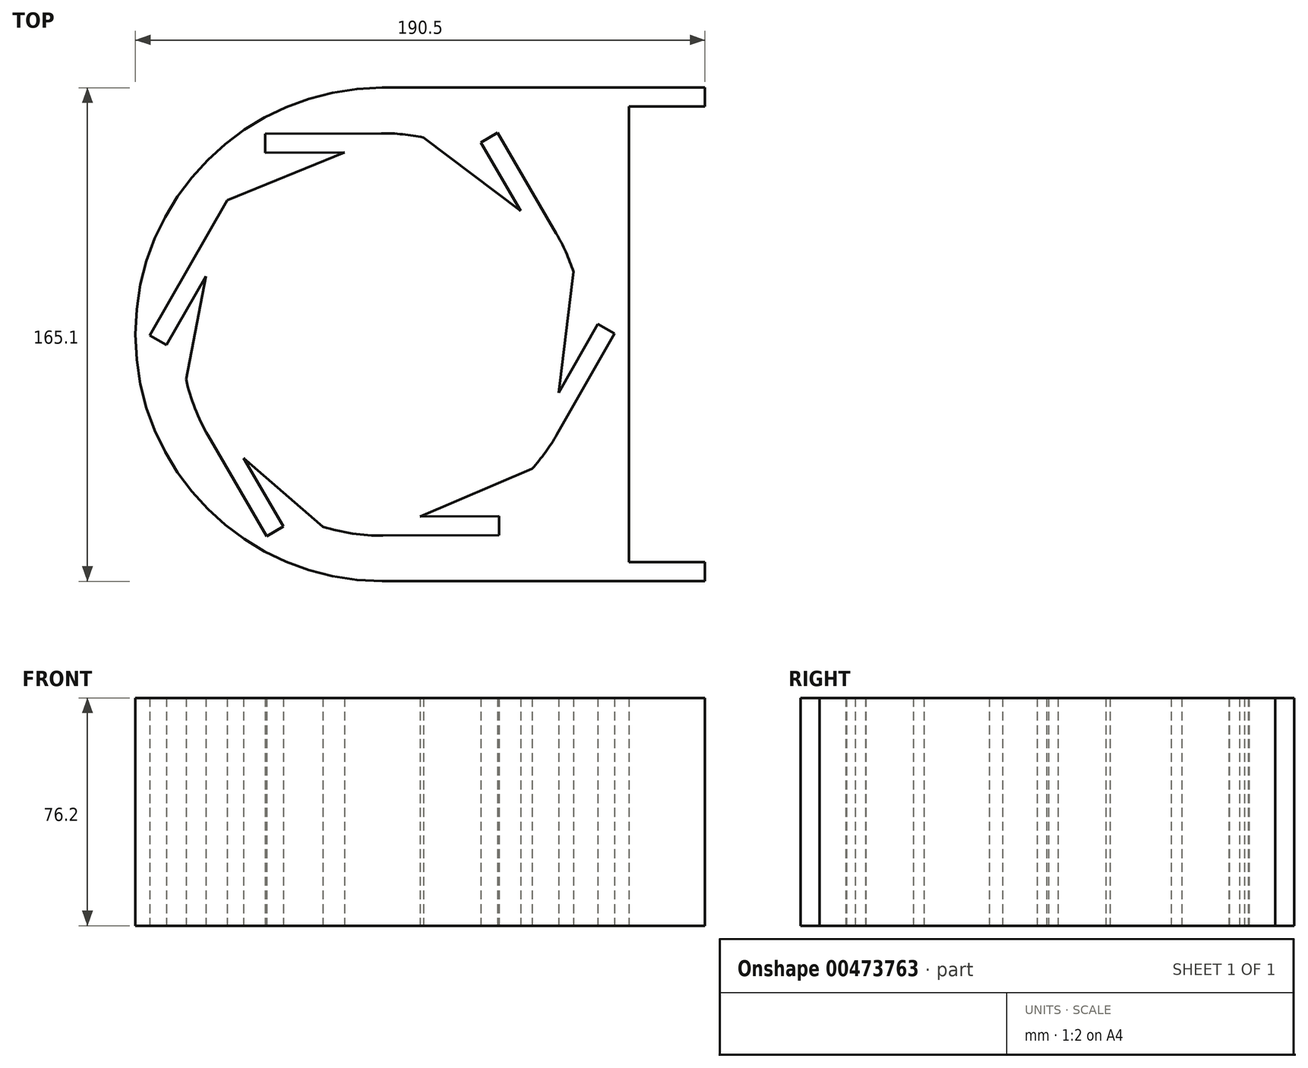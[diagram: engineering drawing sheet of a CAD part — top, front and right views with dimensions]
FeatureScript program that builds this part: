
annotation { "Feature Type Name" : "Feature", "Feature Type Description" : "" }
export const myFeature = defineFeature(function(context is Context, id is Id, definition is map)
    precondition{}
    {
        {
            var Q0;
            Q0=qCreatedBy(makeId("Top.planeOp"),FACE);
            var sketch = newSketch(context, id + "F0", { "sketchPlane" : qUnion([Q0])});
            skArc(sketch, "E0", {"start": v(-65.63, -17.73) * mm, "mid": v(-62.61, -27.48) * mm, "end": v(-58.16, -36.65) * mm});
            skArc(sketch, "E1.cCircle", {"start": v(-65.63, -17.73) * mm, "mid": v(-62.61, -27.48) * mm, "end": v(-58.16, -36.65) * mm, "construction": true});
            skLineSegment(sketch, "E1.0", {"start": v(38.6, 64.7) * mm, "end": v(58.16, 31.12) * mm});
            skLineSegment(sketch, "E1.1", {"start": v(77.72, -2.46) * mm, "end": v(58.42, -36.2) * mm});
            skLineSegment(sketch, "E1.2", {"start": v(39.13, -69.92) * mm, "end": v(0.27, -70.08) * mm});
            skLineSegment(sketch, "E1.3", {"start": v(-38.6, -70.23) * mm, "end": v(-58.16, -36.65) * mm});
            skLineSegment(sketch, "E1.4", {"start": v(-77.72, -3.07) * mm, "end": v(-51.86, 42.14) * mm});
            skLineSegment(sketch, "E1.5", {"start": v(-39.13, 64.39) * mm, "end": v(-0.27, 64.54) * mm});
            skPoint(sketch, "E1.0.midPoint", {"position": v(58.16, 31.12) * mm});
            skLineSegment(sketch, "E2", {"start": v(38.6, 64.7) * mm, "end": v(33.04, 61.46) * mm});
            skLineSegment(sketch, "E3", {"start": v(33.04, 61.46) * mm, "end": v(46.37, 38.6) * mm});
            skLineSegment(sketch, "E4", {"start": v(50.92, 41.25) * mm, "end": v(51.92, 41.83) * mm});
            skLineSegment(sketch, "E5", {"start": v(-39.13, 64.39) * mm, "end": v(-39.1, 57.96) * mm});
            skLineSegment(sketch, "E6", {"start": v(-39.1, 57.96) * mm, "end": v(-12.64, 58.07) * mm});
            skLineSegment(sketch, "E7", {"start": v(-12.64, 63.35) * mm, "end": v(-12.64, 64.5) * mm});
            skLineSegment(sketch, "E8", {"start": v(-12.64, 64.5) * mm, "end": v(-39.13, 64.39) * mm});
            skLineSegment(sketch, "E9", {"start": v(-77.72, -3.07) * mm, "end": v(-72.14, -6.26) * mm});
            skLineSegment(sketch, "E10", {"start": v(-72.14, -6.26) * mm, "end": v(-59, 16.7) * mm});
            skLineSegment(sketch, "E11", {"start": v(-63.58, 19.33) * mm, "end": v(-64.58, 19.9) * mm});
            skLineSegment(sketch, "E12", {"start": v(-38.6, -70.23) * mm, "end": v(-33.04, -67) * mm});
            skLineSegment(sketch, "E13", {"start": v(-33.04, -67) * mm, "end": v(-46.37, -44.13) * mm});
            skLineSegment(sketch, "E14", {"start": v(-50.92, -46.78) * mm, "end": v(-51.92, -47.36) * mm});
            skLineSegment(sketch, "E15", {"start": v(39.13, -69.92) * mm, "end": v(39.1, -63.5) * mm});
            skLineSegment(sketch, "E16", {"start": v(39.1, -63.5) * mm, "end": v(12.64, -63.6) * mm});
            skLineSegment(sketch, "E17", {"start": v(12.66, -68.88) * mm, "end": v(12.66, -70.03) * mm});
            skLineSegment(sketch, "E18", {"start": v(77.72, -2.46) * mm, "end": v(72.14, 0.73) * mm});
            skLineSegment(sketch, "E19", {"start": v(72.14, 0.73) * mm, "end": v(59, -22.24) * mm});
            skLineSegment(sketch, "E20", {"start": v(63.58, -24.86) * mm, "end": v(64.58, -25.43) * mm});
            skArc(sketch, "E21", {"start": v(0, 79.78) * mm, "mid": v(-82.55, -2.77) * mm, "end": v(0, -85.32) * mm});
            skArc(sketch, "E22.trimOffspring", {"start": v(-49.12, 43.25) * mm, "mid": v(-49.64, 42.7) * mm, "end": v(-50.14, 42.14) * mm, "construction": true});
            skArc(sketch, "E23.trimOffspring", {"start": v(13.83, 63.1) * mm, "mid": v(6.82, 64.2) * mm, "end": v(-0.27, 64.54) * mm, "construction": true});
            skArc(sketch, "E24.trimOffspring", {"start": v(13.83, 63.1) * mm, "mid": v(6.82, 64.2) * mm, "end": v(-0.27, 64.54) * mm});
            skArc(sketch, "E25.trimOffspring", {"start": v(-49.12, 43.25) * mm, "mid": v(-49.64, 42.7) * mm, "end": v(-50.14, 42.14) * mm});
            skArc(sketch, "E26.trimOffspring", {"start": v(63.96, 18.2) * mm, "mid": v(61.4, 24.81) * mm, "end": v(58.16, 31.12) * mm, "construction": true});
            skArc(sketch, "E27.trimOffspring", {"start": v(63.96, 18.2) * mm, "mid": v(61.4, 24.81) * mm, "end": v(58.16, 31.12) * mm});
            skArc(sketch, "E28.trimOffspring", {"start": v(50.14, -47.67) * mm, "mid": v(54.59, -42.15) * mm, "end": v(58.42, -36.2) * mm, "construction": true});
            skArc(sketch, "E29.trimOffspring", {"start": v(50.14, -47.67) * mm, "mid": v(54.59, -42.15) * mm, "end": v(58.42, -36.2) * mm});
            skArc(sketch, "E30.trimOffspring", {"start": v(-19.85, -67.08) * mm, "mid": v(-9.9, -69.34) * mm, "end": v(0.27, -70.08) * mm, "construction": true});
            skArc(sketch, "E31.trimOffspring", {"start": v(-19.85, -67.08) * mm, "mid": v(-9.9, -69.34) * mm, "end": v(0.27, -70.08) * mm});
            skLineSegment(sketch, "E32", {"start": v(-12.64, 58.07) * mm, "end": v(-51.86, 42.14) * mm});
            skPoint(sketch, "E32.endSnap0", {"position": v(-50.14, 42.14) * mm});
            skLineSegment(sketch, "E33", {"start": v(-51.86, 42.14) * mm, "end": v(-50.14, 42.14) * mm});
            skLineSegment(sketch, "E34", {"start": v(46.37, 38.6) * mm, "end": v(13.83, 63.1) * mm});
            skLineSegment(sketch, "E35", {"start": v(59, -22.24) * mm, "end": v(63.96, 18.2) * mm});
            skLineSegment(sketch, "E36", {"start": v(12.64, -63.6) * mm, "end": v(50.14, -47.67) * mm});
            skLineSegment(sketch, "E37", {"start": v(-46.37, -44.13) * mm, "end": v(-19.85, -67.08) * mm});
            skLineSegment(sketch, "E38", {"start": v(-59, 16.7) * mm, "end": v(-65.63, -17.73) * mm});
            skLineSegment(sketch, "E39", {"start": v(0, 79.78) * mm, "end": v(82.55, 79.78) * mm});
            skLineSegment(sketch, "E40", {"start": v(82.55, 79.78) * mm, "end": v(82.55, -85.32) * mm});
            skLineSegment(sketch, "E41", {"start": v(82.55, -85.32) * mm, "end": v(0, -85.32) * mm});
            skLineSegment(sketch, "E42.bottom", {"start": v(82.55, -85.32) * mm, "end": v(107.95, -85.32) * mm});
            skLineSegment(sketch, "E42.top", {"start": v(82.55, -78.97) * mm, "end": v(107.95, -78.97) * mm});
            skLineSegment(sketch, "E42.left", {"start": v(82.55, -85.32) * mm, "end": v(82.55, -78.97) * mm});
            skLineSegment(sketch, "E42.right", {"start": v(107.95, -85.32) * mm, "end": v(107.95, -78.97) * mm});
            skLineSegment(sketch, "E43.bottom", {"start": v(82.55, 79.78) * mm, "end": v(107.95, 79.78) * mm});
            skLineSegment(sketch, "E43.top", {"start": v(82.55, 73.43) * mm, "end": v(107.95, 73.43) * mm});
            skLineSegment(sketch, "E43.left", {"start": v(82.55, 79.78) * mm, "end": v(82.55, 73.43) * mm});
            skLineSegment(sketch, "E43.right", {"start": v(107.95, 79.78) * mm, "end": v(107.95, 73.43) * mm});
            skSolve(sketch);
        }
        {
            var Q0;
            Q0 = qSketchRegion(id + "F0", true);
            extrude(context, id + "F1", {"entities" : qUnion([Q0]), "depth" : 76.2 * mm});
        }
    });
